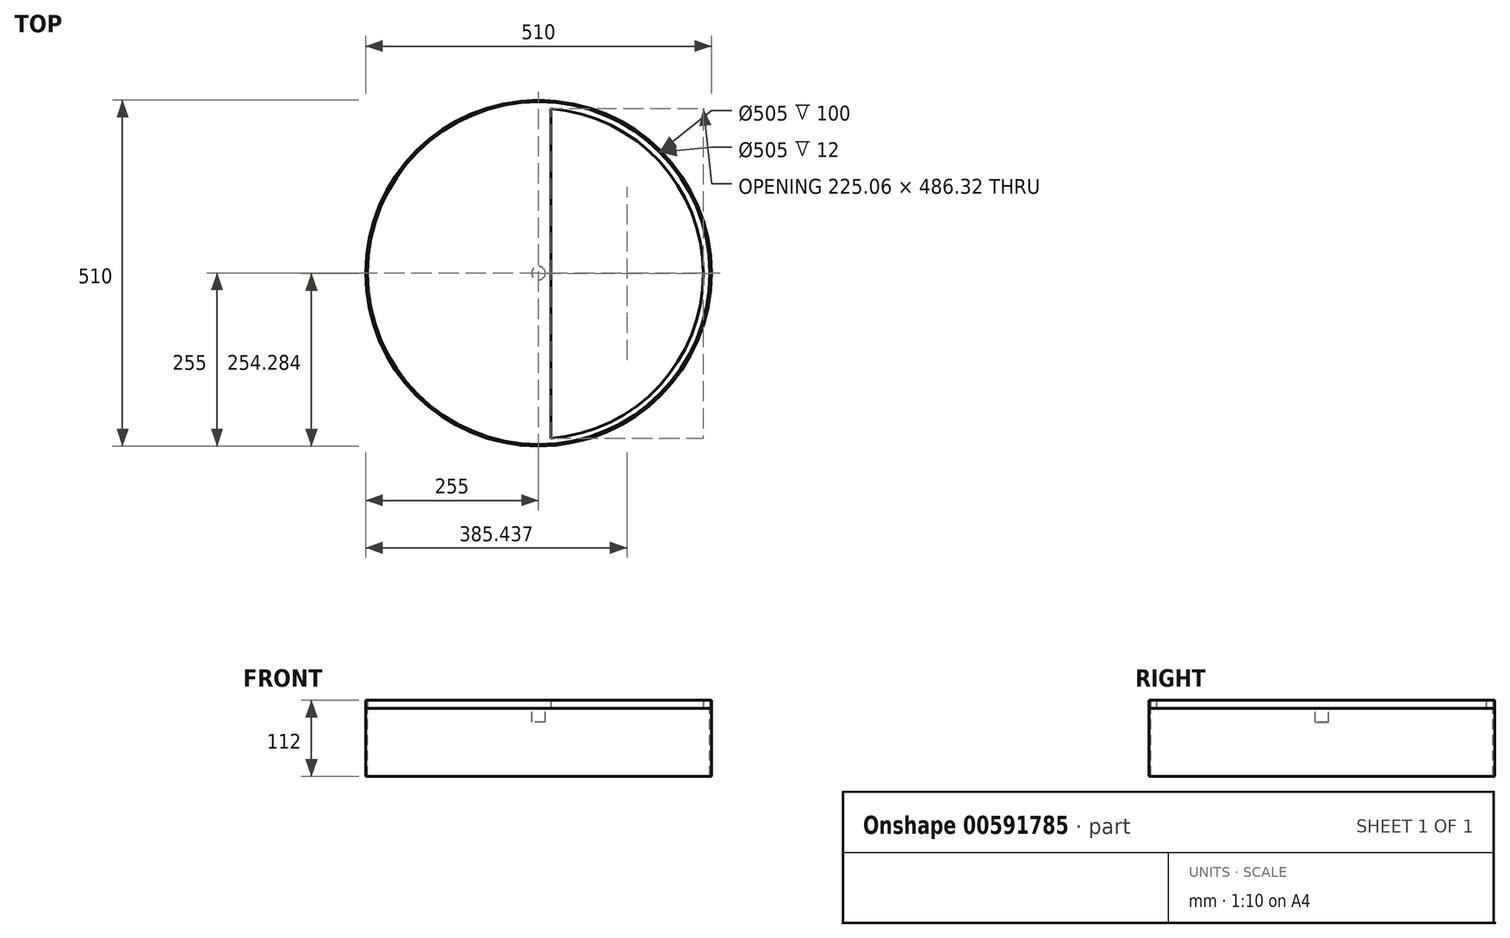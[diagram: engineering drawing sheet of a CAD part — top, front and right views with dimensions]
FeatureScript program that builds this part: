
annotation { "Feature Type Name" : "Feature", "Feature Type Description" : "" }
export const myFeature = defineFeature(function(context is Context, id is Id, definition is map)
    precondition{}
    {
        {
            var Q0;
            Q0=qCreatedBy(makeId("Top.planeOp"),FACE);
            var sketch = newSketch(context, id + "F0", { "sketchPlane" : qUnion([Q0])});
            skCircle(sketch, "E0", {"center": v(0, 0) * mm, "radius": 252.5 * mm});
            skSolve(sketch);
        }
        {
            var Q0;
            Q0=qSketchRegion(id+"F0",true);
            extrude(context, id + "F1", {"entities" : qUnion([Q0]), "depth" : 12 * mm});
        }
        {
            var Q0;
            Q0=qCreatedBy(makeId("Top.planeOp"),FACE);
            var sketch = newSketch(context, id + "F2", { "sketchPlane" : qUnion([Q0])});
            skCircle(sketch, "E1", {"center": v(0, 0) * mm, "radius": 10 * mm});
            skSolve(sketch);
        }
        {
            var Q0;
            Q0=qSketchRegion(id+"F2",true);
            extrude(context, id + "F3", {"entities" : qUnion([Q0]), "operationType" : NewBodyOperationType.ADD, "oppositeDirection" : true, "depth" : 20 * mm});
        }
        {
            var Q0;
            Q0=qCreatedBy(makeId("Top.planeOp"),FACE);
            var sketch = newSketch(context, id + "F4", { "sketchPlane" : qUnion([Q0])});
            skLineSegment(sketch, "E2", {"start": v(17.9, 0) * mm, "end": v(17.9, -243.88) * mm});
            skLineSegment(sketch, "E3", {"start": v(17.9, -243.88) * mm, "end": v(17.9, 242.45) * mm});
            skArc(sketch, "E4", {"start": v(17.9, -243.88) * mm, "mid": v(242.97, -0.72) * mm, "end": v(17.9, 242.45) * mm});
            skSolve(sketch);
        }
        {
            var Q0;
            Q0=qSketchRegion(id+"F4",true);
            extrude(context, id + "F5", {"entities" : qUnion([Q0]), "operationType" : NewBodyOperationType.REMOVE, "depth" : 12 * mm});
        }
        {
            var Q0;
            Q0=qCreatedBy(makeId("Top.planeOp"),FACE);
            var sketch = newSketch(context, id + "F6", { "sketchPlane" : qUnion([Q0])});
            skCircle(sketch, "E5", {"center": v(0, 0) * mm, "radius": 252.5 * mm});
            skCircle(sketch, "E6", {"center": v(0, 0) * mm, "radius": 255 * mm});
            skSolve(sketch);
        }
        {
            var Q0;
            Q0=qSketchRegion(id+"F6",true);
            extrude(context, id + "F7", {"entities" : qUnion([Q0]), "oppositeDirection" : true, "depth" : 100 * mm});
        }
        {
            var Q0;
            Q0=qSketchRegion(id+"F6",true);
            extrude(context, id + "F8", {"entities" : qUnion([Q0]), "depth" : 12 * mm});
        }
    });
